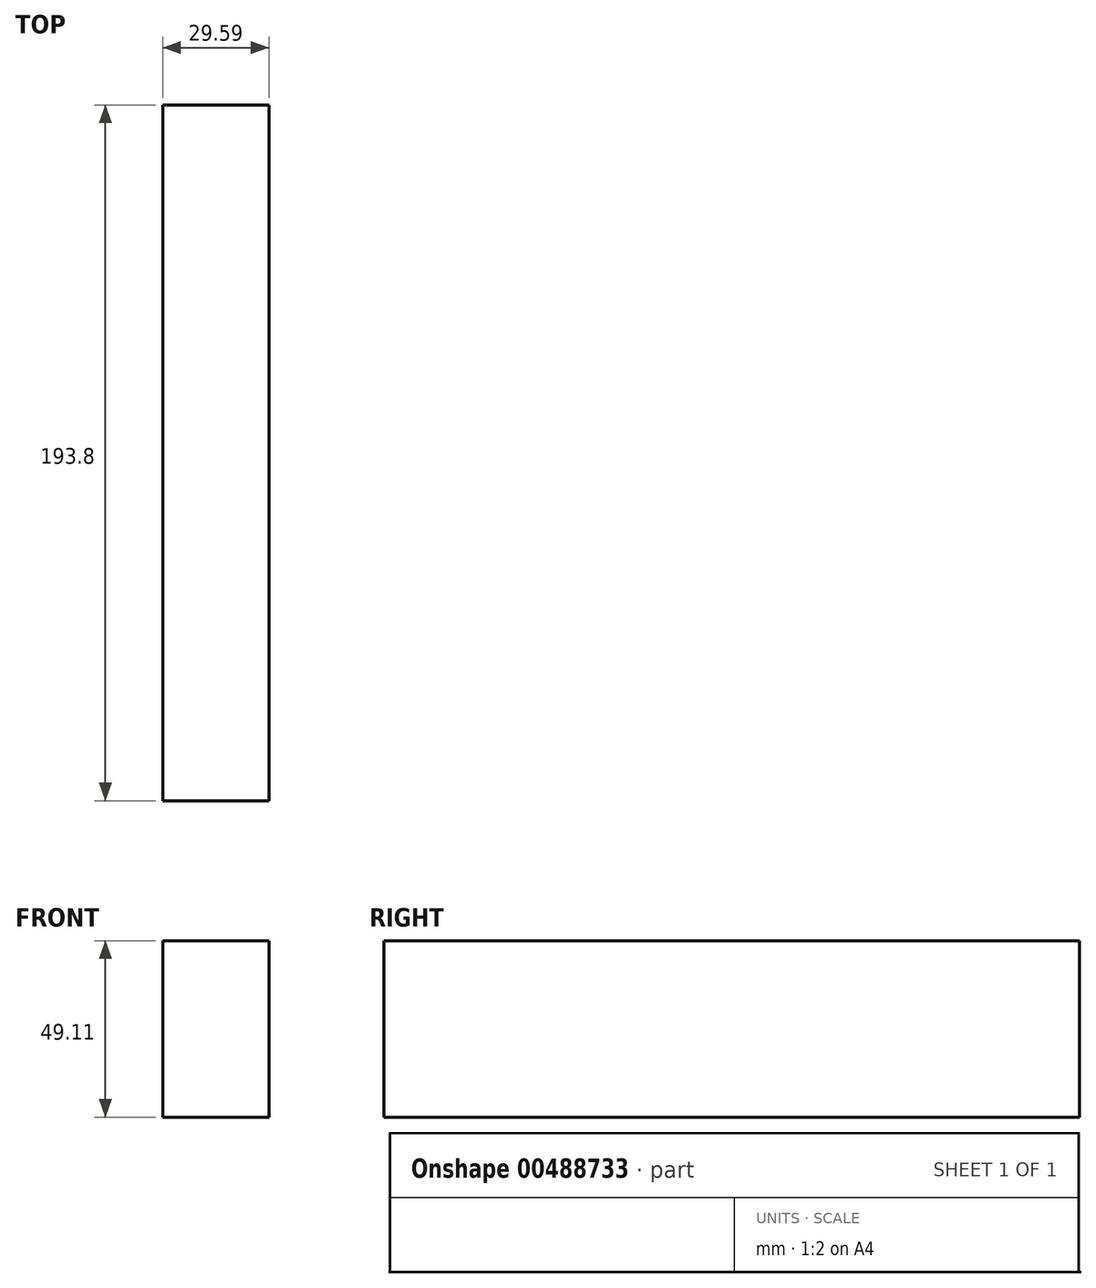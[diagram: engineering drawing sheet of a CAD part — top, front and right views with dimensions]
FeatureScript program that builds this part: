
annotation { "Feature Type Name" : "Feature", "Feature Type Description" : "" }
export const myFeature = defineFeature(function(context is Context, id is Id, definition is map)
    precondition{}
    {
        {
            var Q0;
            Q0=qCreatedBy(makeId("Front.planeOp"),FACE);
            var sketch = newSketch(context, id + "F0", { "sketchPlane" : qUnion([Q0])});
            skLineSegment(sketch, "E0.bottom", {"start": v(-21.96, 30.9) * mm, "end": v(7.63, 30.9) * mm});
            skLineSegment(sketch, "E0.top", {"start": v(-21.96, -18.22) * mm, "end": v(7.63, -18.22) * mm});
            skLineSegment(sketch, "E0.left", {"start": v(-21.96, 30.9) * mm, "end": v(-21.96, -18.22) * mm});
            skLineSegment(sketch, "E0.right", {"start": v(7.63, 30.9) * mm, "end": v(7.63, -18.22) * mm});
            skSolve(sketch);
        }
        {
            var Q0;
            Q0 = qSketchRegion(id + "F0", true);
            extrude(context, id + "F1", {"entities" : qUnion([Q0]), "depth" : 193.8 * mm});
        }
    });
